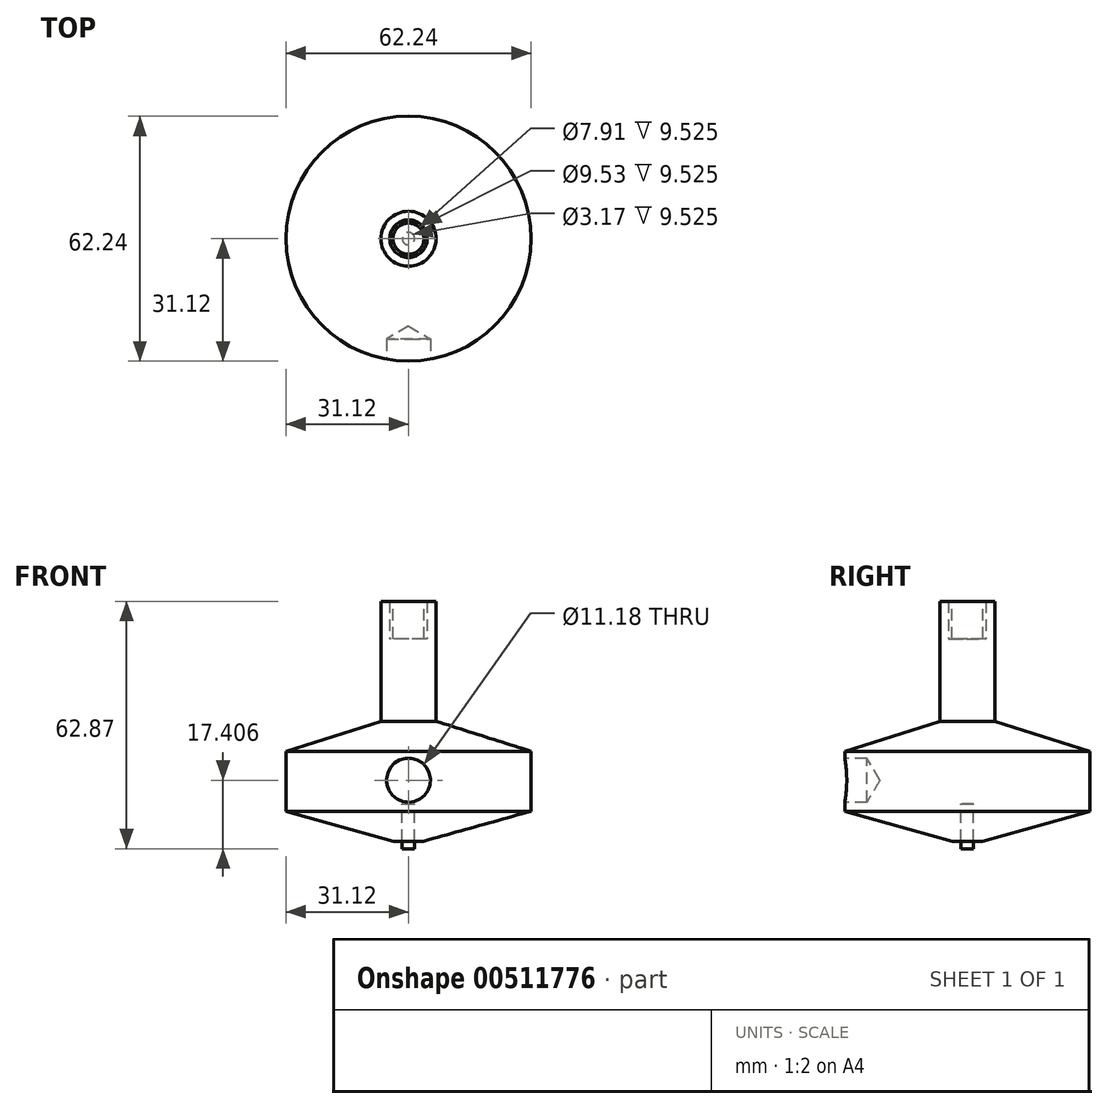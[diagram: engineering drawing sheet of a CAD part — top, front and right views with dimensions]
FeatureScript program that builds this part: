
annotation { "Feature Type Name" : "Feature", "Feature Type Description" : "" }
export const myFeature = defineFeature(function(context is Context, id is Id, definition is map)
    precondition{}
    {
        {
            var Q0;
            Q0=qCreatedBy(makeId("Front.planeOp"),FACE);
            var sketch = newSketch(context, id + "F0", { "sketchPlane" : qUnion([Q0])});
            skLineSegment(sketch, "E0", {"start": v(31.12, 9.53) * mm, "end": v(31.12, 24.77) * mm});
            skLineSegment(sketch, "E1", {"start": v(6.99, 62.87) * mm, "end": v(0, 62.87) * mm});
            skLineSegment(sketch, "E2", {"start": v(0, 62.87) * mm, "end": v(0, 1.9) * mm});
            skLineSegment(sketch, "E3", {"start": v(0, 1.9) * mm, "end": v(3.81, 1.9) * mm});
            skLineSegment(sketch, "E4", {"start": v(3.81, 1.9) * mm, "end": v(31.12, 9.53) * mm});
            skLineSegment(sketch, "E5", {"start": v(31.12, 24.77) * mm, "end": v(6.98, 32.39) * mm});
            skLineSegment(sketch, "E6", {"start": v(6.98, 32.39) * mm, "end": v(6.98, 62.87) * mm});
            skPoint(sketch, "E7", {"position": v(31.12, 17.15) * mm});
            skSolve(sketch);
        }
        {
            var Q0;
            Q0=makeQuery(id+"F0.imprint","IMPRINT",FACE,{"disambiguationData":[TD([[makeQuery(id+"F0.imprint","IMPRINT",EDGE,{"derivedFrom":sQuery(id+"F0.wireOp",EDGE,"E0")}),1.0]])]});
            var Q1;
            Q1=sQuery(id+"F0.wireOp",EDGE,"E2");
            revolve(context, id + "F1", {"entities" : qUnion([Q0]), "axis" : qUnion([Q1]), "revolveType" : RevolveType.FULL});
        }
        {
            var Q0;
            Q0=makeQuery(id+"F1.opRevolve","SWEPT_FACE",FACE,{"disambiguationData":[OSD([sQuery(id+"F0.wireOp",EDGE,"E1")])]});
            var sketch = newSketch(context, id + "F2", { "sketchPlane" : qUnion([Q0])});
            skCircle(sketch, "E8", {"center": v(0, 0) * mm, "radius": 4.76 * mm});
            skSolve(sketch);
        }
        {
            var Q0;
            Q0=makeQuery(id+"F2.imprint","IMPRINT",FACE,{"disambiguationData":[TD([[makeQuery(id+"F2.imprint","IMPRINT",EDGE,{"derivedFrom":sQuery(id+"F2.wireOp",EDGE,"E8")}),1.0]])]});
            extrude(context, id + "F3", {"entities" : qUnion([Q0]), "operationType" : NewBodyOperationType.REMOVE, "oppositeDirection" : true, "depth" : 9.52 * mm});
        }
        {
            var Q0;
            Q0=makeQuery(id+"F1.opRevolve","SWEPT_FACE",FACE,{"disambiguationData":[OSD([sQuery(id+"F0.wireOp",EDGE,"E3")])]});
            var sketch = newSketch(context, id + "F4", { "sketchPlane" : qUnion([Q0])});
            skCircle(sketch, "E9", {"center": v(0, 0) * mm, "radius": 1.59 * mm});
            skSolve(sketch);
        }
        {
            var Q0;
            Q0=qSketchRegion(id+"F4",true);
            extrude(context, id + "F5", {"entities" : qUnion([Q0]), "operationType" : NewBodyOperationType.REMOVE, "oppositeDirection" : true, "depth" : 9.52 * mm});
        }
        {
            var Q0;
            Q0=makeQuery(id+"F3.boolean.opBoolean","COPY",FACE,{"derivedFrom":makeQuery(id+"F3.opExtrude","CAP_FACE",FACE,{"disambiguationData":[OSD([sQuery(id+"F2.wireOp",EDGE,"E8")])],"isStart":false})});
            extrude(context, id + "F6", {"entities" : qUnion([Q0]), "depth" : 9.52 * mm});
        }
        {
            var Q0;
            Q0=makeQuery(id+"F6.opExtrude","CAP_FACE",FACE,{"disambiguationData":[OSD([sQuery(id+"F2.wireOp",EDGE,"E8")])],"isStart":false});
            var sketch = newSketch(context, id + "F7", { "sketchPlane" : qUnion([Q0])});
            skCircle(sketch, "E10", {"center": v(0, 0) * mm, "radius": 3.95 * mm});
            skSolve(sketch);
        }
        {
            var Q0;
            Q0=makeQuery(id+"F7.imprint","IMPRINT",FACE,{"disambiguationData":[TD([[makeQuery(id+"F7.imprint","IMPRINT",EDGE,{"derivedFrom":sQuery(id+"F7.wireOp",EDGE,"E10")}),1.0]])]});
            extrude(context, id + "F8", {"entities" : qUnion([Q0]), "operationType" : NewBodyOperationType.REMOVE, "oppositeDirection" : true, "depth" : 9.52 * mm});
        }
        {
            var Q0;
            Q0=makeQuery(id+"F5.boolean.opBoolean","COPY",FACE,{"derivedFrom":makeQuery(id+"F5.opExtrude","CAP_FACE",FACE,{"disambiguationData":[OSD([sQuery(id+"F4.wireOp",EDGE,"E9")])],"isStart":false})});
            extrude(context, id + "F9", {"entities" : qUnion([Q0]), "depth" : 11.43 * mm});
        }
        {
            var Q0;
            Q0=qCreatedBy(makeId("Front.planeOp"),FACE);
            cPlane(context, id + "F10", {"entities" : qUnion([Q0]), "cplaneType" : CPlaneType.OFFSET, "offset" : 31.12 * mm, "width" : 152.4 * mm, "height" : 152.4 * mm});
        }
        {
            var Q0;
            Q0=qCreatedBy(id+"F10.planeOp",FACE);
            var sketch = newSketch(context, id + "F11", { "sketchPlane" : qUnion([Q0])});
            skCircle(sketch, "E11", {"center": v(0, 17.4) * mm, "radius": 5.74 * mm});
            skSolve(sketch);
        }
        {
            var Q0;
            Q0=sQuery(id+"F11.wireOp",VERTEX,"E11.center");
            var Q1;
            Q1=makeQuery(id+"F1.opRevolve","SWEPT_BODY",BODY,{"disambiguationData":[OSD([sQuery(id+"F0.wireOp",EDGE,"E0"),sQuery(id+"F0.wireOp",EDGE,"E1"),sQuery(id+"F0.wireOp",EDGE,"E2"),sQuery(id+"F0.wireOp",EDGE,"E3"),sQuery(id+"F0.wireOp",EDGE,"E4"),sQuery(id+"F0.wireOp",EDGE,"E5"),sQuery(id+"F0.wireOp",EDGE,"E6")])]});
            hole(context, id + "F12", {"style" : HoleStyle.SIMPLE, "endStyle" : HoleEndStyle.BLIND, "holeDiameter" : 11.18 * mm, "holeDepth" : 5.08 * mm, "isTappedThrough" : true, "tappedDepth" : 12.7 * mm, "tapClearance" : 3, "locations" : qUnion([Q0]), "scope" : qUnion([Q1])});
        }
    });
